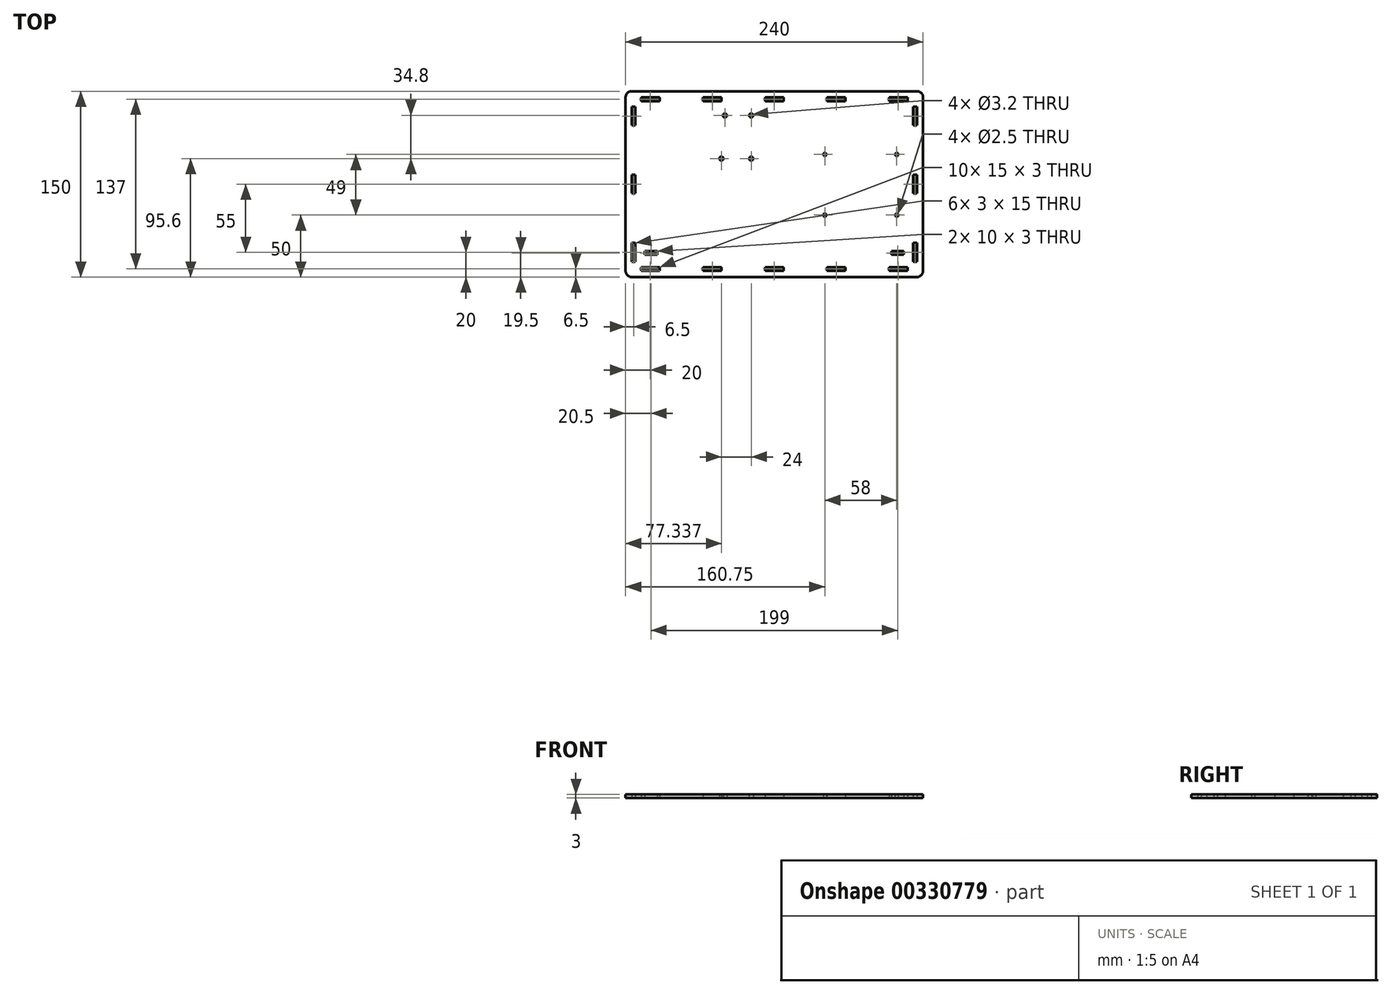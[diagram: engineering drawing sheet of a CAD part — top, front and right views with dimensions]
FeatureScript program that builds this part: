
annotation { "Feature Type Name" : "Feature", "Feature Type Description" : "" }
export const myFeature = defineFeature(function(context is Context, id is Id, definition is map)
    precondition{}
    {
        {
            var Q0;
            Q0=qCreatedBy(makeId("Top.planeOp"),FACE);
            var sketch = newSketch(context, id + "F0", { "sketchPlane" : qUnion([Q0])});
            skLineSegment(sketch, "E0.bottom", {"start": v(115, 75) * mm, "end": v(-115, 75) * mm});
            skLineSegment(sketch, "E0.top", {"start": v(115, -75) * mm, "end": v(-115, -75) * mm});
            skLineSegment(sketch, "E0.left", {"start": v(120, 70) * mm, "end": v(120, -70) * mm});
            skLineSegment(sketch, "E0.right", {"start": v(-120, 70) * mm, "end": v(-120, -70) * mm});
            skPoint(sketch, "E0.middle", {"position": v(0, 0) * mm});
            skLineSegment(sketch, "E1.bottom", {"start": v(-107.5, 70) * mm, "end": v(-92.5, 70) * mm});
            skLineSegment(sketch, "E1.top", {"start": v(-107.5, 67) * mm, "end": v(-92.5, 67) * mm});
            skLineSegment(sketch, "E1.left", {"start": v(-107.5, 70) * mm, "end": v(-107.5, 67) * mm});
            skLineSegment(sketch, "E1.right", {"start": v(-92.5, 70) * mm, "end": v(-92.5, 67) * mm});
            skLineSegment(sketch, "E2.0.1.0", {"start": v(-107.5, -67) * mm, "end": v(-107.5, -70) * mm});
            skLineSegment(sketch, "E2.0.1.1", {"start": v(-107.5, -67) * mm, "end": v(-92.5, -67) * mm});
            skLineSegment(sketch, "E2.0.1.2", {"start": v(-92.5, -67) * mm, "end": v(-92.5, -70) * mm});
            skLineSegment(sketch, "E2.0.1.3", {"start": v(-107.5, -70) * mm, "end": v(-92.5, -70) * mm});
            skLineSegment(sketch, "E2.1.0.0", {"start": v(-57.5, 70) * mm, "end": v(-57.5, 67) * mm});
            skLineSegment(sketch, "E2.1.0.1", {"start": v(-57.5, 70) * mm, "end": v(-42.5, 70) * mm});
            skLineSegment(sketch, "E2.1.0.2", {"start": v(-42.5, 70) * mm, "end": v(-42.5, 67) * mm});
            skLineSegment(sketch, "E2.1.0.3", {"start": v(-57.5, 67) * mm, "end": v(-42.5, 67) * mm});
            skLineSegment(sketch, "E2.1.1.0", {"start": v(-57.5, -67) * mm, "end": v(-57.5, -70) * mm});
            skLineSegment(sketch, "E2.1.1.1", {"start": v(-57.5, -67) * mm, "end": v(-42.5, -67) * mm});
            skLineSegment(sketch, "E2.1.1.2", {"start": v(-42.5, -67) * mm, "end": v(-42.5, -70) * mm});
            skLineSegment(sketch, "E2.1.1.3", {"start": v(-57.5, -70) * mm, "end": v(-42.5, -70) * mm});
            skLineSegment(sketch, "E2.2.0.0", {"start": v(-7.5, 70) * mm, "end": v(-7.5, 67) * mm});
            skLineSegment(sketch, "E2.2.0.1", {"start": v(-7.5, 70) * mm, "end": v(7.5, 70) * mm});
            skLineSegment(sketch, "E2.2.0.2", {"start": v(7.5, 70) * mm, "end": v(7.5, 67) * mm});
            skLineSegment(sketch, "E2.2.0.3", {"start": v(-7.5, 67) * mm, "end": v(7.5, 67) * mm});
            skLineSegment(sketch, "E2.2.1.0", {"start": v(-7.5, -67) * mm, "end": v(-7.5, -70) * mm});
            skLineSegment(sketch, "E2.2.1.1", {"start": v(-7.5, -67) * mm, "end": v(7.5, -67) * mm});
            skLineSegment(sketch, "E2.2.1.2", {"start": v(7.5, -67) * mm, "end": v(7.5, -70) * mm});
            skLineSegment(sketch, "E2.2.1.3", {"start": v(-7.5, -70) * mm, "end": v(7.5, -70) * mm});
            skLineSegment(sketch, "E2.3.0.0", {"start": v(42.5, 70) * mm, "end": v(42.5, 67) * mm});
            skLineSegment(sketch, "E2.3.0.1", {"start": v(42.5, 70) * mm, "end": v(57.5, 70) * mm});
            skLineSegment(sketch, "E2.3.0.2", {"start": v(57.5, 70) * mm, "end": v(57.5, 67) * mm});
            skLineSegment(sketch, "E2.3.0.3", {"start": v(42.5, 67) * mm, "end": v(57.5, 67) * mm});
            skLineSegment(sketch, "E2.3.1.0", {"start": v(42.5, -67) * mm, "end": v(42.5, -70) * mm});
            skLineSegment(sketch, "E2.3.1.1", {"start": v(42.5, -67) * mm, "end": v(57.5, -67) * mm});
            skLineSegment(sketch, "E2.3.1.2", {"start": v(57.5, -67) * mm, "end": v(57.5, -70) * mm});
            skLineSegment(sketch, "E2.3.1.3", {"start": v(42.5, -70) * mm, "end": v(57.5, -70) * mm});
            skLineSegment(sketch, "E2.direction1", {"start": v(-107.5, 67) * mm, "end": v(-57.5, 67) * mm, "construction": true});
            skLineSegment(sketch, "E2.direction2", {"start": v(-107.5, 67) * mm, "end": v(-107.5, -70) * mm, "construction": true});
            skLineSegment(sketch, "E3.0.4.0", {"start": v(92.5, 70) * mm, "end": v(92.5, 67) * mm});
            skLineSegment(sketch, "E3.3.4.0", {"start": v(92.5, 70) * mm, "end": v(107.5, 70) * mm});
            skLineSegment(sketch, "E3.6.4.0", {"start": v(107.5, 70) * mm, "end": v(107.5, 67) * mm});
            skLineSegment(sketch, "E3.9.4.0", {"start": v(92.5, 67) * mm, "end": v(107.5, 67) * mm});
            skLineSegment(sketch, "E3.0.4.1", {"start": v(92.5, -67) * mm, "end": v(92.5, -70) * mm});
            skLineSegment(sketch, "E3.3.4.1", {"start": v(92.5, -67) * mm, "end": v(107.5, -67) * mm});
            skLineSegment(sketch, "E3.6.4.1", {"start": v(107.5, -67) * mm, "end": v(107.5, -70) * mm});
            skLineSegment(sketch, "E3.9.4.1", {"start": v(92.5, -70) * mm, "end": v(107.5, -70) * mm});
            skPoint(sketch, "E4.visualSharp", {"position": v(-120, 75) * mm});
            skArc(sketch, "E4.filletArc", {"start": v(-115, 75) * mm, "mid": v(-118.54, 73.54) * mm, "end": v(-120, 70) * mm});
            skPoint(sketch, "E5.visualSharp", {"position": v(-120, -75) * mm});
            skArc(sketch, "E5.filletArc", {"start": v(-120, -70) * mm, "mid": v(-118.54, -73.54) * mm, "end": v(-115, -75) * mm});
            skPoint(sketch, "E6.visualSharp", {"position": v(120, -75) * mm});
            skArc(sketch, "E6.filletArc", {"start": v(115, -75) * mm, "mid": v(118.54, -73.54) * mm, "end": v(120, -70) * mm});
            skPoint(sketch, "E7.visualSharp", {"position": v(120, 75) * mm});
            skArc(sketch, "E7.filletArc", {"start": v(120, 70) * mm, "mid": v(118.54, 73.54) * mm, "end": v(115, 75) * mm});
            skLineSegment(sketch, "E8.bottom", {"start": v(112, 62.5) * mm, "end": v(115, 62.5) * mm});
            skLineSegment(sketch, "E8.top", {"start": v(112, 47.5) * mm, "end": v(115, 47.5) * mm});
            skLineSegment(sketch, "E8.left", {"start": v(112, 62.5) * mm, "end": v(112, 47.5) * mm});
            skLineSegment(sketch, "E8.right", {"start": v(115, 62.5) * mm, "end": v(115, 47.5) * mm});
            skLineSegment(sketch, "E9.0.1.0", {"start": v(112, 7.5) * mm, "end": v(115, 7.5) * mm});
            skLineSegment(sketch, "E9.0.1.1", {"start": v(115, 7.5) * mm, "end": v(115, -7.5) * mm});
            skLineSegment(sketch, "E9.0.1.2", {"start": v(112, -7.5) * mm, "end": v(115, -7.5) * mm});
            skLineSegment(sketch, "E9.0.1.3", {"start": v(112, 7.5) * mm, "end": v(112, -7.5) * mm});
            skLineSegment(sketch, "E9.0.2.0", {"start": v(112, -47.5) * mm, "end": v(115, -47.5) * mm});
            skLineSegment(sketch, "E9.0.2.1", {"start": v(115, -47.5) * mm, "end": v(115, -62.5) * mm});
            skLineSegment(sketch, "E9.0.2.2", {"start": v(112, -62.5) * mm, "end": v(115, -62.5) * mm});
            skLineSegment(sketch, "E9.0.2.3", {"start": v(112, -47.5) * mm, "end": v(112, -62.5) * mm});
            skLineSegment(sketch, "E9.1.0.0", {"start": v(-115, 62.5) * mm, "end": v(-112, 62.5) * mm});
            skLineSegment(sketch, "E9.1.0.1", {"start": v(-112, 62.5) * mm, "end": v(-112, 47.5) * mm});
            skLineSegment(sketch, "E9.1.0.2", {"start": v(-115, 47.5) * mm, "end": v(-112, 47.5) * mm});
            skLineSegment(sketch, "E9.1.0.3", {"start": v(-115, 62.5) * mm, "end": v(-115, 47.5) * mm});
            skLineSegment(sketch, "E9.1.1.0", {"start": v(-115, 7.5) * mm, "end": v(-112, 7.5) * mm});
            skLineSegment(sketch, "E9.1.1.1", {"start": v(-112, 7.5) * mm, "end": v(-112, -7.5) * mm});
            skLineSegment(sketch, "E9.1.1.2", {"start": v(-115, -7.5) * mm, "end": v(-112, -7.5) * mm});
            skLineSegment(sketch, "E9.1.1.3", {"start": v(-115, 7.5) * mm, "end": v(-115, -7.5) * mm});
            skLineSegment(sketch, "E9.1.2.0", {"start": v(-115, -47.5) * mm, "end": v(-112, -47.5) * mm});
            skLineSegment(sketch, "E9.1.2.1", {"start": v(-112, -47.5) * mm, "end": v(-112, -62.5) * mm});
            skLineSegment(sketch, "E9.1.2.2", {"start": v(-115, -62.5) * mm, "end": v(-112, -62.5) * mm});
            skLineSegment(sketch, "E9.1.2.3", {"start": v(-115, -47.5) * mm, "end": v(-115, -62.5) * mm});
            skLineSegment(sketch, "E9.direction1", {"start": v(112, 62.5) * mm, "end": v(-115, 62.5) * mm, "construction": true});
            skLineSegment(sketch, "E9.direction2", {"start": v(112, 62.5) * mm, "end": v(112, 7.5) * mm, "construction": true});
            skLineSegment(sketch, "E10.bottom", {"start": v(-104.5, -54) * mm, "end": v(-94.5, -54) * mm});
            skLineSegment(sketch, "E10.top", {"start": v(-104.5, -57) * mm, "end": v(-94.5, -57) * mm});
            skLineSegment(sketch, "E10.left", {"start": v(-104.5, -54) * mm, "end": v(-104.5, -57) * mm});
            skLineSegment(sketch, "E10.right", {"start": v(-94.5, -54) * mm, "end": v(-94.5, -57) * mm});
            skLineSegment(sketch, "E11.bottom", {"start": v(104.5, -57) * mm, "end": v(94.5, -57) * mm});
            skLineSegment(sketch, "E11.top", {"start": v(104.5, -54) * mm, "end": v(94.5, -54) * mm});
            skLineSegment(sketch, "E11.left", {"start": v(104.5, -57) * mm, "end": v(104.5, -54) * mm});
            skLineSegment(sketch, "E11.right", {"start": v(94.5, -57) * mm, "end": v(94.5, -54) * mm});
            skCircle(sketch, "E12", {"center": v(-39.86, 55.4) * mm, "radius": 1.6 * mm});
            skCircle(sketch, "E13", {"center": v(-18.66, 55.4) * mm, "radius": 1.6 * mm});
            skCircle(sketch, "E14", {"center": v(-42.66, 20.6) * mm, "radius": 1.6 * mm});
            skCircle(sketch, "E15", {"center": v(-18.66, 20.6) * mm, "radius": 1.6 * mm});
            skCircle(sketch, "E16", {"center": v(40.75, 24) * mm, "radius": 1.25 * mm});
            skCircle(sketch, "E17", {"center": v(98.75, 24) * mm, "radius": 1.25 * mm});
            skCircle(sketch, "E18", {"center": v(40.75, -25) * mm, "radius": 1.25 * mm});
            skCircle(sketch, "E19", {"center": v(98.75, -25) * mm, "radius": 1.25 * mm});
            skSolve(sketch);
        }
        {
            var Q0;
            Q0=makeQuery(id+"F0.imprint","IMPRINT",FACE,{"disambiguationData":[TD([[makeQuery(id+"F0.imprint","IMPRINT",EDGE,{"derivedFrom":sQuery(id+"F0.wireOp",EDGE,"E0.bottom")}),1.0]])]});
            extrude(context, id + "F1", {"entities" : qUnion([Q0]), "depth" : 3 * mm});
        }
    });
